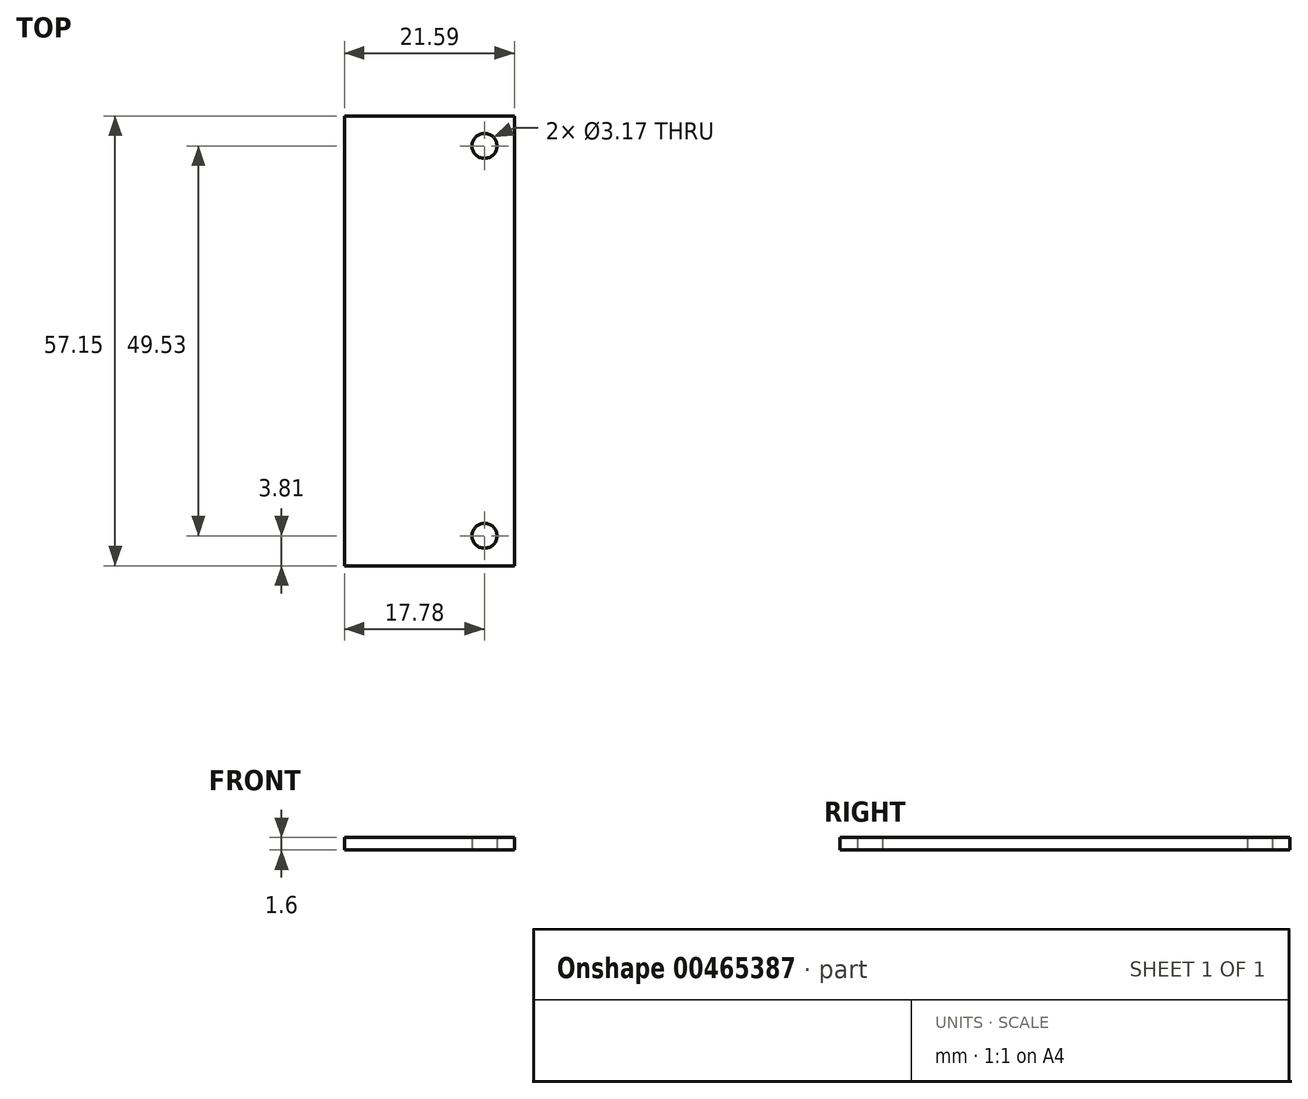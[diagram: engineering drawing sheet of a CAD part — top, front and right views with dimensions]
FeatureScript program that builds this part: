
annotation { "Feature Type Name" : "Feature", "Feature Type Description" : "" }
export const myFeature = defineFeature(function(context is Context, id is Id, definition is map)
    precondition{}
    {
        {
            var Q0;
            Q0=qCreatedBy(makeId("Top.planeOp"),FACE);
            var sketch = newSketch(context, id + "F0", { "sketchPlane" : qUnion([Q0])});
            skLineSegment(sketch, "E0.bottom", {"start": v(0, 0) * mm, "end": v(21.59, 0) * mm});
            skLineSegment(sketch, "E0.top", {"start": v(0, -57.15) * mm, "end": v(21.6, -57.15) * mm});
            skLineSegment(sketch, "E0.left", {"start": v(0, 0) * mm, "end": v(0, -57.15) * mm});
            skLineSegment(sketch, "E0.right", {"start": v(21.59, 0) * mm, "end": v(21.59, -57.15) * mm});
            skCircle(sketch, "E1", {"center": v(17.78, -3.81) * mm, "radius": 1.59 * mm});
            skCircle(sketch, "E2", {"center": v(17.78, -53.34) * mm, "radius": 1.59 * mm});
            skSolve(sketch);
        }
        {
            var Q0;
            Q0=makeQuery(id+"F0.imprint","IMPRINT",FACE,{"disambiguationData":[TD([[makeQuery(id+"F0.imprint","IMPRINT",EDGE,{"derivedFrom":sQuery(id+"F0.wireOp",EDGE,"E0.bottom")}),-1.0]])]});
            extrude(context, id + "F1", {"entities" : qUnion([Q0]), "depth" : 1.6 * mm, "offsetDistance" : 25 * mm});
        }
    });
